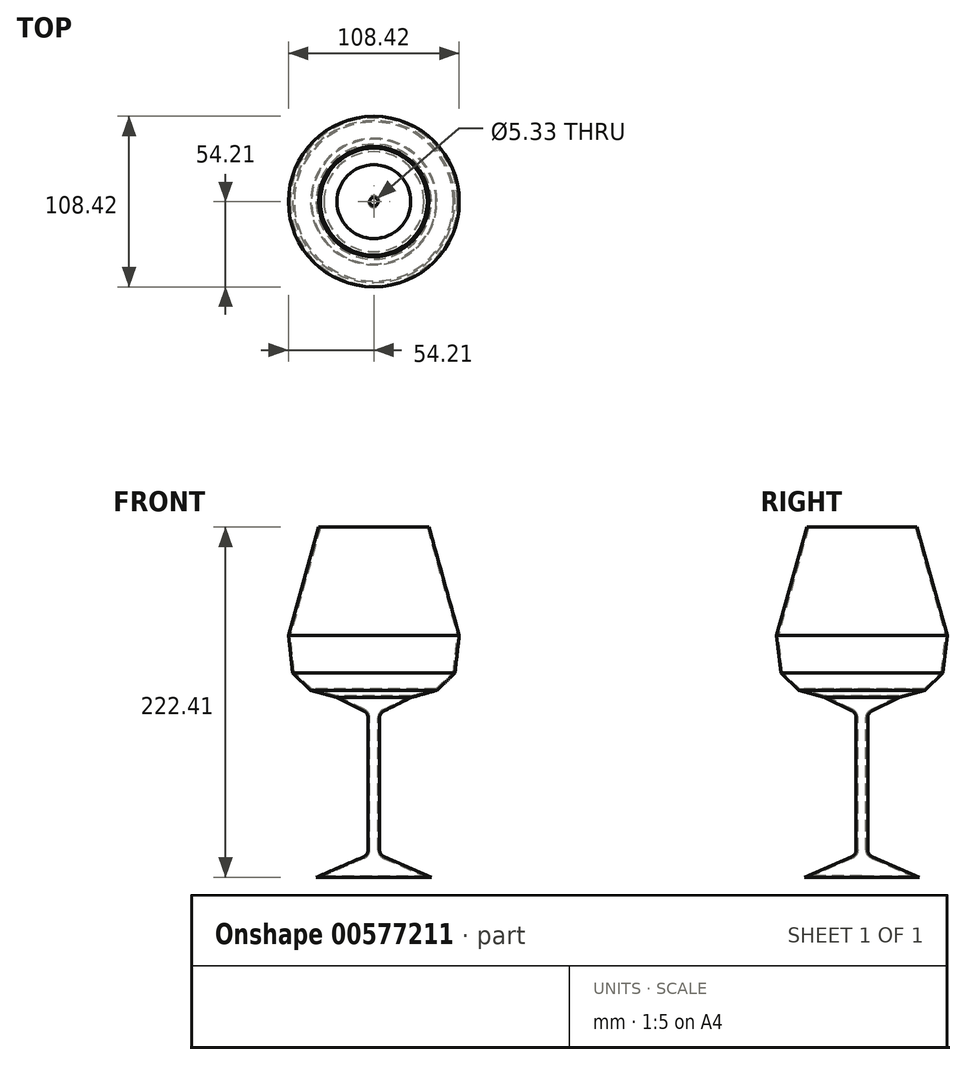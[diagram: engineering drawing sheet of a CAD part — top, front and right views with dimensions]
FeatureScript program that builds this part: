
annotation { "Feature Type Name" : "Feature", "Feature Type Description" : "" }
export const myFeature = defineFeature(function(context is Context, id is Id, definition is map)
    precondition{}
    {
        {
            var Q0;
            Q0=qCreatedBy(makeId("Front.planeOp"),FACE);
            var sketch = newSketch(context, id + "F0", { "sketchPlane" : qUnion([Q0])});
            skLineSegment(sketch, "E0", {"start": v(-35, 120) * mm, "end": v(0, 120) * mm});
            skLineSegment(sketch, "E1", {"start": v(-35, 120) * mm, "end": v(-54.21, 51.13) * mm});
            skLineSegment(sketch, "E2", {"start": v(-54.21, 51.13) * mm, "end": v(-51.49, 27.2) * mm});
            skLineSegment(sketch, "E3", {"start": v(-51.49, 27.2) * mm, "end": v(-40.1, 16.32) * mm});
            skLineSegment(sketch, "E4", {"start": v(-40.1, 16.32) * mm, "end": v(-23.8, 11.77) * mm});
            skLineSegment(sketch, "E5", {"start": v(-23.8, 11.77) * mm, "end": v(0, 0) * mm});
            skLineSegment(sketch, "E6", {"start": v(-3.66, 1.81) * mm, "end": v(-3.66, -88.19) * mm});
            skLineSegment(sketch, "E7", {"start": v(-3.66, -88.19) * mm, "end": v(-36.57, -102.4) * mm});
            skLineSegment(sketch, "E8", {"start": v(0, -102.4) * mm, "end": v(-36.57, -102.4) * mm});
            skLineSegment(sketch, "E9", {"start": v(0, 120) * mm, "end": v(0, -102.4) * mm});
            skSolve(sketch);
        }
        {
            var Q0;
            Q0 = qSketchRegion(id + "F0", true);
            var Q1;
            Q1=sQuery(id+"F0.wireOp",EDGE,"E9");
            revolve(context, id + "F1", {"entities" : qUnion([Q0]), "axis" : qUnion([Q1]), "revolveType" : RevolveType.FULL});
        }
        {
            var Q0;
            Q0=makeQuery(id+"F1.opRevolve","SWEPT_EDGE",EDGE,{"disambiguationData":[OSD([sQuery(id+"F0.wireOp",EDGE,"E5"),sQuery(id+"F0.wireOp",EDGE,"E6")])]});
            var Q1;
            Q1=makeQuery(id+"F1.opRevolve","SWEPT_EDGE",EDGE,{"disambiguationData":[OSD([sQuery(id+"F0.wireOp",EDGE,"E6"),sQuery(id+"F0.wireOp",EDGE,"E7")])]});
            fillet(context, id + "F2", {"entities" : qUnion([Q0, Q1]), "radius" : 5 * mm, "tangentPropagation" : true, "allowEdgeOverflow" : false});
        }
        {
            var Q0;
            Q0=makeQuery(id+"F1.opRevolve","SWEPT_FACE",FACE,{"disambiguationData":[OSD([sQuery(id+"F0.wireOp",EDGE,"E0")])]});
            shell(context, id + "F3", {"entities" : qUnion([Q0]), "thickness" : 1 * mm});
        }
    });
